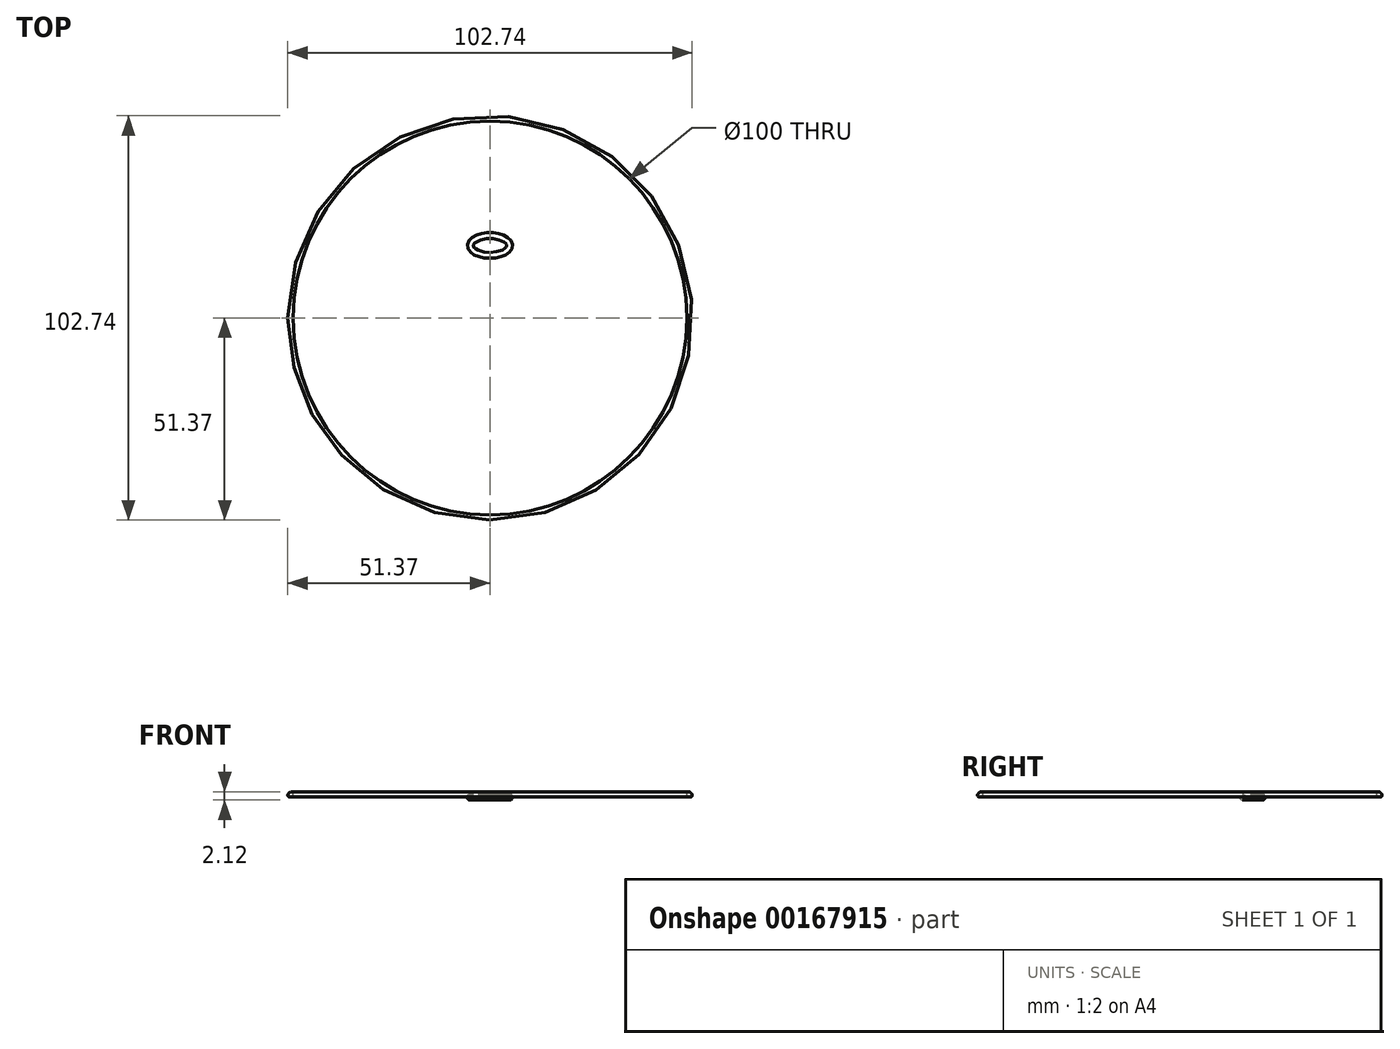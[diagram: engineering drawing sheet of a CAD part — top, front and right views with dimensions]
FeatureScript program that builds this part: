
annotation { "Feature Type Name" : "Feature", "Feature Type Description" : "" }
export const myFeature = defineFeature(function(context is Context, id is Id, definition is map)
    precondition{}
    {
        {
            var Q0;
            Q0=qCreatedBy(makeId("Top.planeOp"),FACE);
            var sketch = newSketch(context, id + "F0", { "sketchPlane" : qUnion([Q0])});
            skCircle(sketch, "E0", {"center": v(0, 0) * mm, "radius": 50 * mm});
            skSolve(sketch);
        }
        {
            var Q0;
            Q0=qCreatedBy(makeId("Front.planeOp"),FACE);
            var sketch = newSketch(context, id + "F1", { "sketchPlane" : qUnion([Q0])});
            skLineSegment(sketch, "E1.0", {"start": v(-50, 0) * mm, "end": v(50, 0) * mm});
            skLineSegment(sketch, "E2", {"start": v(50, 0) * mm, "end": v(50, 1.5) * mm});
            skArc(sketch, "E3", {"start": v(51.5, 0) * mm, "mid": v(51.06, 1.06) * mm, "end": v(50, 1.5) * mm});
            skLineSegment(sketch, "E4", {"start": v(50, 0) * mm, "end": v(51.5, 0) * mm});
            skSolve(sketch);
        }
        {
            var Q0;
            Q0=makeQuery(id+"F1.imprint","IMPRINT",FACE,{"disambiguationData":[TD([[makeQuery(id+"F1.imprint","IMPRINT",EDGE,{"derivedFrom":sQuery(id+"F1.wireOp",EDGE,"E2")}),-1.0]])]});
            var Q1;
            Q1=sQuery(id+"F0.wireOp",EDGE,"E0");
            sweep(context, id + "F2", {"profiles" : qUnion([Q0]), "path" : qUnion([Q1])});
        }
        {
            var Q0;
            Q0=makeQuery(id+"F2.opSweep","SWEPT_EDGE",EDGE,{"disambiguationData":[OSD([sQuery(id+"F0.wireOp",EDGE,"E0"),sQuery(id+"F1.wireOp",EDGE,"E2"),sQuery(id+"F1.wireOp",EDGE,"E3")])]});
            var Q1;
            Q1=makeQuery(id+"F2.opSweep","SWEPT_EDGE",EDGE,{"disambiguationData":[OSD([sQuery(id+"F0.wireOp",EDGE,"E0"),sQuery(id+"F1.wireOp",EDGE,"E3"),sQuery(id+"F1.wireOp",EDGE,"E4")])]});
            var Q2;
            Q2=makeQuery(id+"F2.opSweep","SWEPT_EDGE",EDGE,{"disambiguationData":[OSD([sQuery(id+"F0.wireOp",EDGE,"E0"),sQuery(id+"F1.wireOp",EDGE,"E2"),sQuery(id+"F1.wireOp",EDGE,"E4")])]});
            fillet(context, id + "F3", {"entities" : qUnion([Q0, Q1, Q2]), "radius" : 0.5 * mm, "tangentPropagation" : true, "allowEdgeOverflow" : false});
        }
        {
            var Q0;
            Q0=qCreatedBy(makeId("Top.planeOp"),FACE);
            var sketch = newSketch(context, id + "F4", { "sketchPlane" : qUnion([Q0])});
            skArc(sketch, "E5", {"start": v(0, 18.42) * mm, "mid": v(13.03, -13.03) * mm, "end": v(-18.42, 0) * mm});
            skEllipse(sketch, "E6", {"center": v(0, 18.42) * mm, "majorRadius": 5 * mm, "minorRadius": 2.5 * mm, "majorAxis": v(-1, 0)});
            skSolve(sketch);
        }
        {
            var Q0;
            Q0=qCreatedBy(makeId("Front.planeOp"),FACE);
            var sketch = newSketch(context, id + "F5", { "sketchPlane" : qUnion([Q0])});
            skLineSegment(sketch, "E7.0", {"start": v(18.42, 0) * mm, "end": v(-18.42, 0) * mm});
            skCircle(sketch, "E8", {"center": v(-18.42, 0) * mm, "radius": 0.75 * mm});
            skSolve(sketch);
        }
        {
            var Q0;
            Q0=makeQuery(id+"F5.imprint","IMPRINT",FACE,{"disambiguationData":[TD([[makeQuery(id+"F5.imprint","IMPRINT",EDGE,{"derivedFrom":sQuery(id+"F5.wireOp",EDGE,"E8")}),1.0]])]});
            var Q1;
            Q1=sQuery(id+"F4.wireOp",EDGE,"E5");
            sweep(context, id + "F6", {"profiles" : qUnion([Q0]), "path" : qUnion([Q1])});
        }
        {
            var Q0;
            Q0=makeQuery(id+"F6.opSweep","CAP_FACE",FACE,{"disambiguationData":[OSD([sQuery(id+"F4.wireOp",VERTEX,"E5.start"),sQuery(id+"F5.wireOp",EDGE,"E8")])],"isStart":false});
            var sketch = newSketch(context, id + "F7", { "sketchPlane" : qUnion([Q0])});
            skLineSegment(sketch, "E9.0", {"start": v(-20.92, 0) * mm, "end": v(-15.92, 0) * mm});
            skCircle(sketch, "E10", {"center": v(-15.92, 0) * mm, "radius": 0.75 * mm});
            skSolve(sketch);
        }
        {
            var Q0;
            Q0=makeQuery(id+"F7.imprint","IMPRINT",FACE,{"disambiguationData":[TD([[makeQuery(id+"F7.imprint","IMPRINT",EDGE,{"derivedFrom":sQuery(id+"F7.wireOp",EDGE,"E10")}),1.0]])]});
            var Q1;
            Q1=sQuery(id+"F4.wireOp",EDGE,"E6");
            sweep(context, id + "F8", {"profiles" : qUnion([Q0]), "path" : qUnion([Q1])});
        }
        {
            var Q0;
            Q0=makeQuery(id+"F6.opSweep","SWEPT_BODY",BODY,{"disambiguationData":[OSD([sQuery(id+"F4.wireOp",EDGE,"E5"),sQuery(id+"F5.wireOp",EDGE,"E8")])]});
            var Q1;
            Q1=makeQuery(id+"F8.opSweep","SWEPT_BODY",BODY,{"disambiguationData":[OSD([sQuery(id+"F4.wireOp",EDGE,"E6"),sQuery(id+"F7.wireOp",EDGE,"E10")])]});
            booleanBodies(context, id + "F9", {"operationType" : BooleanOperationType.INTERSECTION, "tools" : qUnion([Q0, Q1]), "keepTools" : true});
        }
        {
            var Q0;
            Q0=makeQuery(id+"F9.opBoolean","INTERSECT",BODY,{"derivedFrom":[makeQuery(id+"F6.opSweep","SWEPT_BODY",BODY,{"disambiguationData":[OSD([sQuery(id+"F4.wireOp",EDGE,"E5"),sQuery(id+"F5.wireOp",EDGE,"E8")])]}),makeQuery(id+"F8.opSweep","SWEPT_BODY",BODY,{"disambiguationData":[OSD([sQuery(id+"F4.wireOp",EDGE,"E6"),sQuery(id+"F7.wireOp",EDGE,"E10")])]})]});
            var Q1;
            Q1=makeQuery(id+"F6.opSweep","SWEPT_BODY",BODY,{"disambiguationData":[OSD([sQuery(id+"F4.wireOp",EDGE,"E5"),sQuery(id+"F5.wireOp",EDGE,"E8")])]});
            booleanBodies(context, id + "F10", {"operationType" : BooleanOperationType.SUBTRACTION, "tools" : qUnion([Q0]), "targets" : qUnion([Q1])});
        }
        {
            var Q0;
            Q0=makeQuery(id+"F10.opBoolean","SPLIT",BODY,{"disambiguationData":[OD(0.0)],"derivedFrom":makeQuery(id+"F6.opSweep","SWEPT_BODY",BODY,{"disambiguationData":[OSD([sQuery(id+"F4.wireOp",EDGE,"E5"),sQuery(id+"F5.wireOp",EDGE,"E8")])]})});
            deleteBodies(context, id + "F11", {"entities" : qUnion([Q0])});
        }
    });
